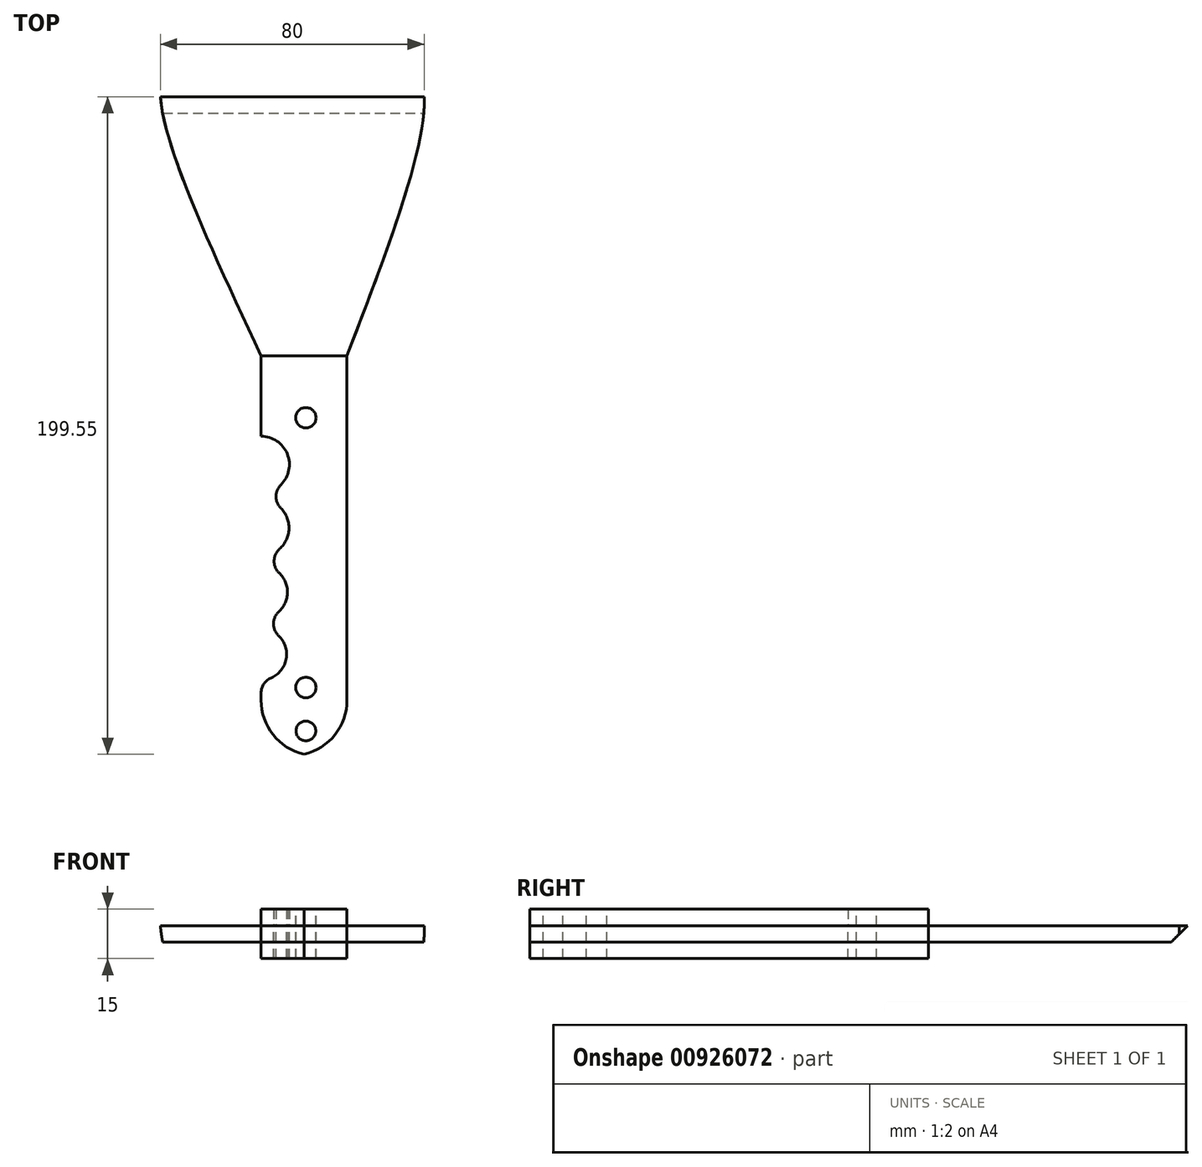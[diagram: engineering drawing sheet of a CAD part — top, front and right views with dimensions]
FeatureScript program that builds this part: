
annotation { "Feature Type Name" : "Feature", "Feature Type Description" : "" }
export const myFeature = defineFeature(function(context is Context, id is Id, definition is map)
    precondition{}
    {
        {
            var Q0;
            Q0=qCreatedBy(makeId("Top.planeOp"),FACE);
            var sketch = newSketch(context, id + "F0", { "sketchPlane" : qUnion([Q0])});
            skLineSegment(sketch, "E0.bottom", {"start": v(-44.1, 124.73) * mm, "end": v(35.9, 124.73) * mm});
            skLineSegment(sketch, "E0.top", {"start": v(-44.1, -75.27) * mm, "end": v(35.9, -75.27) * mm});
            skLineSegment(sketch, "E0.left", {"start": v(-44.1, 124.73) * mm, "end": v(-44.1, -75.27) * mm});
            skLineSegment(sketch, "E0.right", {"start": v(35.9, 124.73) * mm, "end": v(35.9, -75.27) * mm});
            skLineSegment(sketch, "E1", {"start": v(-44.1, 46.13) * mm, "end": v(35.9, 46.13) * mm});
            skLineSegment(sketch, "E2", {"start": v(-13.6, 46.13) * mm, "end": v(-13.6, -75.27) * mm});
            skLineSegment(sketch, "E3", {"start": v(12.5, 46.13) * mm, "end": v(12.5, -75.27) * mm});
            skFitSpline(sketch, "E4", {"points": [v(-13.6, 46.13) * mm, v(-44.1, 124.73) * mm, v(-40.75, 138.68) * mm], "startDerivative": vector(-62.4, 133.41) * mm, "endDerivative": vector(19.43, 38.51) * mm});
            skFitSpline(sketch, "E5", {"points": [v(12.5, 46.13) * mm, v(35.9, 124.73) * mm, v(30.2, 139.37) * mm], "startDerivative": vector(51.9, 135.59) * mm, "endDerivative": vector(-26.75, 38.2) * mm});
            skSolve(sketch);
        }
        {
            var Q0;
            {var subQ1=sQuery(id+"F0.wireOp",EDGE,"E0.bottom");Q0=makeQuery(id+"F0.imprint","IMPRINT",FACE,{"disambiguationData":[TD([[makeQuery(id+"F0.imprint","IMPRINT",EDGE,{"derivedFrom":subQ1}),-1.0]])]});}
            var Q1;
            {var subQ0=sQuery(id+"F0.wireOp",EDGE,"E2");Q1=makeQuery(id+"F0.imprint","IMPRINT",FACE,{"disambiguationData":[TD([[makeQuery(id+"F0.imprint","IMPRINT",EDGE,{"derivedFrom":subQ0}),1.0]])]});}
            extrude(context, id + "F1", {"entities" : qUnion([Q0, Q1]), "depth" : 5 * mm, "offsetDistance" : 25 * mm});
        }
        {
            var Q0;
            Q0=makeQuery(id+"F1.opExtrude","SWEPT_EDGE",EDGE,{"disambiguationData":[OSD([sQuery(id+"F0.wireOp",EDGE,"E0.top"),sQuery(id+"F0.wireOp",EDGE,"E2")])]});
            var Q1;
            Q1=makeQuery(id+"F1.opExtrude","SWEPT_EDGE",EDGE,{"disambiguationData":[OSD([sQuery(id+"F0.wireOp",EDGE,"E0.top"),sQuery(id+"F0.wireOp",EDGE,"E3")])]});
            fillet(context, id + "F2", {"entities" : qUnion([Q0, Q1]), "radius" : 16.9 * mm, "tangentPropagation" : true, "allowEdgeOverflow" : false});
        }
        {
            var Q0;
            Q0=makeQuery(id+"F1.opExtrude","CAP_FACE",FACE,{"disambiguationData":[OSD([sQuery(id+"F0.wireOp",EDGE,"E0.bottom"),sQuery(id+"F0.wireOp",EDGE,"E0.top"),sQuery(id+"F0.wireOp",EDGE,"E0.right"),sQuery(id+"F0.wireOp",EDGE,"E2"),sQuery(id+"F0.wireOp",EDGE,"E3"),sQuery(id+"F0.wireOp",EDGE,"E4"),sQuery(id+"F0.wireOp",EDGE,"E5")])],"isStart":false});
            var sketch = newSketch(context, id + "F3", { "sketchPlane" : qUnion([Q0])});
            skCircle(sketch, "E6", {"center": v(-13.6, -44.48) * mm, "radius": 7.77 * mm});
            skCircle(sketch, "E7", {"center": v(-13.6, -25.63) * mm, "radius": 8 * mm});
            skCircle(sketch, "E8", {"center": v(-13.6, -6.12) * mm, "radius": 8.49 * mm});
            skCircle(sketch, "E9", {"center": v(-13.6, 13.12) * mm, "radius": 8.6 * mm});
            skSolve(sketch);
        }
        {
            var Q0;
            {var subQ0=sQuery(id+"F3.wireOp",EDGE,"E6");var subQ1=makeQuery(id+"F1.opExtrude","CAP_EDGE",EDGE,{"disambiguationData":[OSD([sQuery(id+"F0.wireOp",EDGE,"E2")])],"isStart":false});var subQ2=makeQuery(id+"F3.imprint","INTERSECT",VERTEX,{"disambiguationData":[OD(0.0)],"derivedFrom":[subQ1,subQ0]});Q0=makeQuery(id+"F3.imprint","IMPRINT",FACE,{"disambiguationData":[TD([[makeQuery(id+"F3.imprint","IMPRINT",EDGE,{"disambiguationData":[TD([[subQ2,-1.0]])],"derivedFrom":subQ0}),1.0]])]});}
            var Q1;
            {var subQ0=sQuery(id+"F3.wireOp",EDGE,"E7");var subQ1=makeQuery(id+"F1.opExtrude","CAP_EDGE",EDGE,{"disambiguationData":[OSD([sQuery(id+"F0.wireOp",EDGE,"E2")])],"isStart":false});var subQ2=makeQuery(id+"F3.imprint","INTERSECT",VERTEX,{"disambiguationData":[OD(0.0)],"derivedFrom":[subQ1,subQ0]});Q1=makeQuery(id+"F3.imprint","IMPRINT",FACE,{"disambiguationData":[TD([[makeQuery(id+"F3.imprint","IMPRINT",EDGE,{"disambiguationData":[TD([[subQ2,-1.0]])],"derivedFrom":subQ0}),1.0]])]});}
            var Q2;
            {var subQ0=sQuery(id+"F3.wireOp",EDGE,"E8");var subQ1=makeQuery(id+"F1.opExtrude","CAP_EDGE",EDGE,{"disambiguationData":[OSD([sQuery(id+"F0.wireOp",EDGE,"E2")])],"isStart":false});var subQ2=makeQuery(id+"F3.imprint","INTERSECT",VERTEX,{"disambiguationData":[OD(0.0)],"derivedFrom":[subQ1,subQ0]});Q2=makeQuery(id+"F3.imprint","IMPRINT",FACE,{"disambiguationData":[TD([[makeQuery(id+"F3.imprint","IMPRINT",EDGE,{"disambiguationData":[TD([[subQ2,1.0]])],"derivedFrom":subQ0}),1.0]])]});}
            var Q3;
            {var subQ0=sQuery(id+"F3.wireOp",EDGE,"E9");var subQ1=makeQuery(id+"F1.opExtrude","CAP_EDGE",EDGE,{"disambiguationData":[OSD([sQuery(id+"F0.wireOp",EDGE,"E2")])],"isStart":false});var subQ2=makeQuery(id+"F3.imprint","INTERSECT",VERTEX,{"disambiguationData":[OD(0.0)],"derivedFrom":[subQ1,subQ0]});Q3=makeQuery(id+"F3.imprint","IMPRINT",FACE,{"disambiguationData":[TD([[makeQuery(id+"F3.imprint","IMPRINT",EDGE,{"disambiguationData":[TD([[subQ2,1.0]])],"derivedFrom":subQ0}),1.0]])]});}
            extrude(context, id + "F4", {"entities" : qUnion([Q0, Q1, Q2, Q3]), "operationType" : NewBodyOperationType.REMOVE, "oppositeDirection" : true, "depth" : 25 * mm, "offsetDistance" : 25 * mm});
        }
        {
            var Q0;
            {var subQ0=sQuery(id+"F3.wireOp",EDGE,"E6");var subQ1=sQuery(id+"F0.wireOp",EDGE,"E2");Q0=makeQuery(id+"F4.boolean.opBoolean","COPY",EDGE,{"derivedFrom":makeQuery(id+"F4.opExtrude","SWEPT_EDGE",EDGE,{"disambiguationData":[OSD([subQ1,subQ0]),TDD([makeQuery(id+"F3.imprint","INTERSECT",VERTEX,{"disambiguationData":[OD(1.0)],"derivedFrom":[makeQuery(id+"F1.opExtrude","CAP_EDGE",EDGE,{"disambiguationData":[OSD([subQ1])],"isStart":false}),subQ0]})])]})});}
            fillet(context, id + "F5", {"entities" : qUnion([Q0]), "radius" : 5 * mm, "tangentPropagation" : true, "allowEdgeOverflow" : false});
        }
        {
            var Q0;
            {var subQ0=sQuery(id+"F3.wireOp",EDGE,"E6");var subQ1=sQuery(id+"F0.wireOp",EDGE,"E2");Q0=makeQuery(id+"F5.opFillet","BLEND_EDGE",EDGE,{"blendedFrom":[makeQuery(id+"F4.boolean.opBoolean","COPY",EDGE,{"derivedFrom":makeQuery(id+"F4.opExtrude","SWEPT_EDGE",EDGE,{"disambiguationData":[OSD([subQ1,subQ0]),TDD([makeQuery(id+"F3.imprint","INTERSECT",VERTEX,{"disambiguationData":[OD(1.0)],"derivedFrom":[makeQuery(id+"F1.opExtrude","CAP_EDGE",EDGE,{"disambiguationData":[OSD([subQ1])],"isStart":false}),subQ0]})])]})}),makeQuery(id+"F4.boolean.opBoolean","COPY",FACE,{"derivedFrom":makeQuery(id+"F4.opExtrude","SWEPT_FACE",FACE,{"disambiguationData":[OSD([sQuery(id+"F3.wireOp",EDGE,"E7")])]})})],"blendedInto":[makeQuery(id+"F4.boolean.opBoolean","COPY",FACE,{"derivedFrom":makeQuery(id+"F4.opExtrude","SWEPT_FACE",FACE,{"disambiguationData":[OSD([sQuery(id+"F3.wireOp",EDGE,"E7")])]})})]});}
            fillet(context, id + "F6", {"entities" : qUnion([Q0]), "radius" : 5 * mm, "tangentPropagation" : true, "allowEdgeOverflow" : false});
        }
        {
            var Q0;
            {var subQ0=sQuery(id+"F3.wireOp",EDGE,"E6");var subQ1=sQuery(id+"F0.wireOp",EDGE,"E2");Q0=makeQuery(id+"F4.boolean.opBoolean","COPY",EDGE,{"derivedFrom":makeQuery(id+"F4.opExtrude","SWEPT_EDGE",EDGE,{"disambiguationData":[OSD([subQ1,subQ0]),TDD([makeQuery(id+"F3.imprint","INTERSECT",VERTEX,{"disambiguationData":[OD(0.0)],"derivedFrom":[makeQuery(id+"F1.opExtrude","CAP_EDGE",EDGE,{"disambiguationData":[OSD([subQ1])],"isStart":false}),subQ0]})])]})});}
            fillet(context, id + "F7", {"entities" : qUnion([Q0]), "radius" : 5 * mm, "tangentPropagation" : true, "allowEdgeOverflow" : false});
        }
        {
            var Q0;
            {var subQ0=sQuery(id+"F3.wireOp",EDGE,"E7");var subQ1=sQuery(id+"F0.wireOp",EDGE,"E2");Q0=makeQuery(id+"F4.boolean.opBoolean","COPY",EDGE,{"derivedFrom":makeQuery(id+"F4.opExtrude","SWEPT_EDGE",EDGE,{"disambiguationData":[OSD([subQ1,subQ0]),TDD([makeQuery(id+"F3.imprint","INTERSECT",VERTEX,{"disambiguationData":[OD(1.0)],"derivedFrom":[makeQuery(id+"F1.opExtrude","CAP_EDGE",EDGE,{"disambiguationData":[OSD([subQ1])],"isStart":false}),subQ0]})])]})});}
            fillet(context, id + "F8", {"entities" : qUnion([Q0]), "radius" : 5 * mm, "tangentPropagation" : true, "allowEdgeOverflow" : false});
        }
        {
            var Q0;
            {var subQ0=sQuery(id+"F3.wireOp",EDGE,"E7");var subQ1=sQuery(id+"F0.wireOp",EDGE,"E2");Q0=makeQuery(id+"F8.opFillet","BLEND_EDGE",EDGE,{"blendedFrom":[makeQuery(id+"F4.boolean.opBoolean","COPY",EDGE,{"derivedFrom":makeQuery(id+"F4.opExtrude","SWEPT_EDGE",EDGE,{"disambiguationData":[OSD([subQ1,subQ0]),TDD([makeQuery(id+"F3.imprint","INTERSECT",VERTEX,{"disambiguationData":[OD(1.0)],"derivedFrom":[makeQuery(id+"F1.opExtrude","CAP_EDGE",EDGE,{"disambiguationData":[OSD([subQ1])],"isStart":false}),subQ0]})])]})}),makeQuery(id+"F4.boolean.opBoolean","COPY",FACE,{"derivedFrom":makeQuery(id+"F4.opExtrude","SWEPT_FACE",FACE,{"disambiguationData":[OSD([sQuery(id+"F3.wireOp",EDGE,"E8")])]})})],"blendedInto":[makeQuery(id+"F4.boolean.opBoolean","COPY",FACE,{"derivedFrom":makeQuery(id+"F4.opExtrude","SWEPT_FACE",FACE,{"disambiguationData":[OSD([sQuery(id+"F3.wireOp",EDGE,"E8")])]})})]});}
            fillet(context, id + "F9", {"entities" : qUnion([Q0]), "radius" : 5 * mm, "tangentPropagation" : true, "allowEdgeOverflow" : false});
        }
        {
            var Q0;
            {var subQ0=sQuery(id+"F3.wireOp",EDGE,"E8");var subQ1=sQuery(id+"F0.wireOp",EDGE,"E2");Q0=makeQuery(id+"F4.boolean.opBoolean","COPY",EDGE,{"derivedFrom":makeQuery(id+"F4.opExtrude","SWEPT_EDGE",EDGE,{"disambiguationData":[OSD([subQ1,subQ0]),TDD([makeQuery(id+"F3.imprint","INTERSECT",VERTEX,{"disambiguationData":[OD(0.0)],"derivedFrom":[makeQuery(id+"F1.opExtrude","CAP_EDGE",EDGE,{"disambiguationData":[OSD([subQ1])],"isStart":false}),subQ0]})])]})});}
            fillet(context, id + "F10", {"entities" : qUnion([Q0]), "radius" : 5 * mm, "tangentPropagation" : true, "allowEdgeOverflow" : false});
        }
        {
            var Q0;
            {var subQ0=sQuery(id+"F3.wireOp",EDGE,"E8");var subQ1=sQuery(id+"F0.wireOp",EDGE,"E2");Q0=makeQuery(id+"F10.opFillet","BLEND_EDGE",EDGE,{"blendedFrom":[makeQuery(id+"F4.boolean.opBoolean","COPY",EDGE,{"derivedFrom":makeQuery(id+"F4.opExtrude","SWEPT_EDGE",EDGE,{"disambiguationData":[OSD([subQ1,subQ0]),TDD([makeQuery(id+"F3.imprint","INTERSECT",VERTEX,{"disambiguationData":[OD(0.0)],"derivedFrom":[makeQuery(id+"F1.opExtrude","CAP_EDGE",EDGE,{"disambiguationData":[OSD([subQ1])],"isStart":false}),subQ0]})])]})}),makeQuery(id+"F4.boolean.opBoolean","COPY",FACE,{"derivedFrom":makeQuery(id+"F4.opExtrude","SWEPT_FACE",FACE,{"disambiguationData":[OSD([sQuery(id+"F3.wireOp",EDGE,"E9")])]})})],"blendedInto":[makeQuery(id+"F4.boolean.opBoolean","COPY",FACE,{"derivedFrom":makeQuery(id+"F4.opExtrude","SWEPT_FACE",FACE,{"disambiguationData":[OSD([sQuery(id+"F3.wireOp",EDGE,"E9")])]})})]});}
            fillet(context, id + "F11", {"entities" : qUnion([Q0]), "radius" : 5 * mm, "tangentPropagation" : true, "allowEdgeOverflow" : false});
        }
        {
            var Q0;
            Q0=makeQuery(id+"F1.opExtrude","CAP_FACE",FACE,{"disambiguationData":[OSD([sQuery(id+"F0.wireOp",EDGE,"E0.bottom"),sQuery(id+"F0.wireOp",EDGE,"E0.top"),sQuery(id+"F0.wireOp",EDGE,"E0.right"),sQuery(id+"F0.wireOp",EDGE,"E2"),sQuery(id+"F0.wireOp",EDGE,"E3"),sQuery(id+"F0.wireOp",EDGE,"E4"),sQuery(id+"F0.wireOp",EDGE,"E5")])],"isStart":false});
            var sketch = newSketch(context, id + "F12", { "sketchPlane" : qUnion([Q0])});
            skLineSegment(sketch, "E10", {"start": v(-13.6, 46.13) * mm, "end": v(12.5, 46.13) * mm});
            skSolve(sketch);
        }
        {
            var Q0;
            Q0=makeQuery(id+"F12.imprint","IMPRINT",FACE,{"disambiguationData":[TD([[makeQuery(id+"F12.imprint","IMPRINT",EDGE,{"derivedFrom":sQuery(id+"F12.wireOp",EDGE,"E10")}),-1.0]])]});
            extrude(context, id + "F13", {"entities" : qUnion([Q0]), "depth" : 5 * mm, "offsetDistance" : 25 * mm});
        }
        {
            var Q0;
            Q0=makeQuery(id+"F1.opExtrude","CAP_FACE",FACE,{"disambiguationData":[OSD([sQuery(id+"F0.wireOp",EDGE,"E0.bottom"),sQuery(id+"F0.wireOp",EDGE,"E0.top"),sQuery(id+"F0.wireOp",EDGE,"E0.right"),sQuery(id+"F0.wireOp",EDGE,"E2"),sQuery(id+"F0.wireOp",EDGE,"E3"),sQuery(id+"F0.wireOp",EDGE,"E4"),sQuery(id+"F0.wireOp",EDGE,"E5")])],"isStart":true});
            var sketch = newSketch(context, id + "F14", { "sketchPlane" : qUnion([Q0])});
            skLineSegment(sketch, "E11", {"start": v(12.5, -46.13) * mm, "end": v(-13.6, -46.13) * mm});
            skSolve(sketch);
        }
        {
            var Q0;
            Q0=makeQuery(id+"F14.imprint","IMPRINT",FACE,{"disambiguationData":[TD([[makeQuery(id+"F14.imprint","IMPRINT",EDGE,{"derivedFrom":sQuery(id+"F14.wireOp",EDGE,"E11")}),-1.0]])]});
            extrude(context, id + "F15", {"entities" : qUnion([Q0]), "depth" : 5 * mm, "offsetDistance" : 25 * mm});
        }
        {
            var Q0;
            Q0=makeQuery(id+"F13.opExtrude","CAP_FACE",FACE,{"disambiguationData":[OSD([sQuery(id+"F0.wireOp",EDGE,"E0.bottom"),sQuery(id+"F0.wireOp",EDGE,"E0.top"),sQuery(id+"F0.wireOp",EDGE,"E0.right"),sQuery(id+"F0.wireOp",EDGE,"E2"),sQuery(id+"F0.wireOp",EDGE,"E3"),sQuery(id+"F0.wireOp",EDGE,"E4"),sQuery(id+"F0.wireOp",EDGE,"E5"),sQuery(id+"F3.wireOp",EDGE,"E6"),sQuery(id+"F3.wireOp",EDGE,"E7"),sQuery(id+"F3.wireOp",EDGE,"E8"),sQuery(id+"F3.wireOp",EDGE,"E9"),sQuery(id+"F12.wireOp",EDGE,"E10")])],"isStart":false});
            var sketch = newSketch(context, id + "F16", { "sketchPlane" : qUnion([Q0])});
            skCircle(sketch, "E12", {"center": v(0, 27.32) * mm, "radius": 3.1 * mm});
            skCircle(sketch, "E13", {"center": v(0, -54.55) * mm, "radius": 3.1 * mm});
            skSolve(sketch);
        }
        {
            var Q0;
            Q0=makeQuery(id+"F16.imprint","IMPRINT",FACE,{"disambiguationData":[TD([[makeQuery(id+"F16.imprint","IMPRINT",EDGE,{"derivedFrom":sQuery(id+"F16.wireOp",EDGE,"E13")}),1.0]])]});
            var Q1;
            Q1=makeQuery(id+"F16.imprint","IMPRINT",FACE,{"disambiguationData":[TD([[makeQuery(id+"F16.imprint","IMPRINT",EDGE,{"derivedFrom":sQuery(id+"F16.wireOp",EDGE,"E12")}),1.0]])]});
            extrude(context, id + "F17", {"entities" : qUnion([Q0, Q1]), "operationType" : NewBodyOperationType.REMOVE, "oppositeDirection" : true, "depth" : 25 * mm, "offsetDistance" : 25 * mm});
        }
        {
            var Q0;
            Q0=makeQuery(id+"F13.opExtrude","CAP_FACE",FACE,{"disambiguationData":[OSD([sQuery(id+"F0.wireOp",EDGE,"E0.bottom"),sQuery(id+"F0.wireOp",EDGE,"E0.top"),sQuery(id+"F0.wireOp",EDGE,"E0.right"),sQuery(id+"F0.wireOp",EDGE,"E2"),sQuery(id+"F0.wireOp",EDGE,"E3"),sQuery(id+"F0.wireOp",EDGE,"E4"),sQuery(id+"F0.wireOp",EDGE,"E5"),sQuery(id+"F3.wireOp",EDGE,"E6"),sQuery(id+"F3.wireOp",EDGE,"E7"),sQuery(id+"F3.wireOp",EDGE,"E8"),sQuery(id+"F3.wireOp",EDGE,"E9"),sQuery(id+"F12.wireOp",EDGE,"E10")])],"isStart":false});
            var sketch = newSketch(context, id + "F18", { "sketchPlane" : qUnion([Q0])});
            skCircle(sketch, "E14", {"center": v(0, -67.73) * mm, "radius": 3 * mm});
            skSolve(sketch);
        }
        {
            var Q0;
            Q0=makeQuery(id+"F18.imprint","IMPRINT",FACE,{"disambiguationData":[TD([[makeQuery(id+"F18.imprint","IMPRINT",EDGE,{"derivedFrom":sQuery(id+"F18.wireOp",EDGE,"E14")}),1.0]])]});
            extrude(context, id + "F19", {"entities" : qUnion([Q0]), "operationType" : NewBodyOperationType.REMOVE, "oppositeDirection" : true, "depth" : 25 * mm, "offsetDistance" : 25 * mm});
        }
        {
            var Q0;
            Q0=makeQuery(id+"F1.opExtrude","CAP_EDGE",EDGE,{"disambiguationData":[OSD([sQuery(id+"F0.wireOp",EDGE,"E0.bottom")])],"isStart":true});
            chamfer(context, id + "F20", {"entities" : qUnion([Q0]), "width" : 5 * mm, "tangentPropagation" : true});
        }
    });
